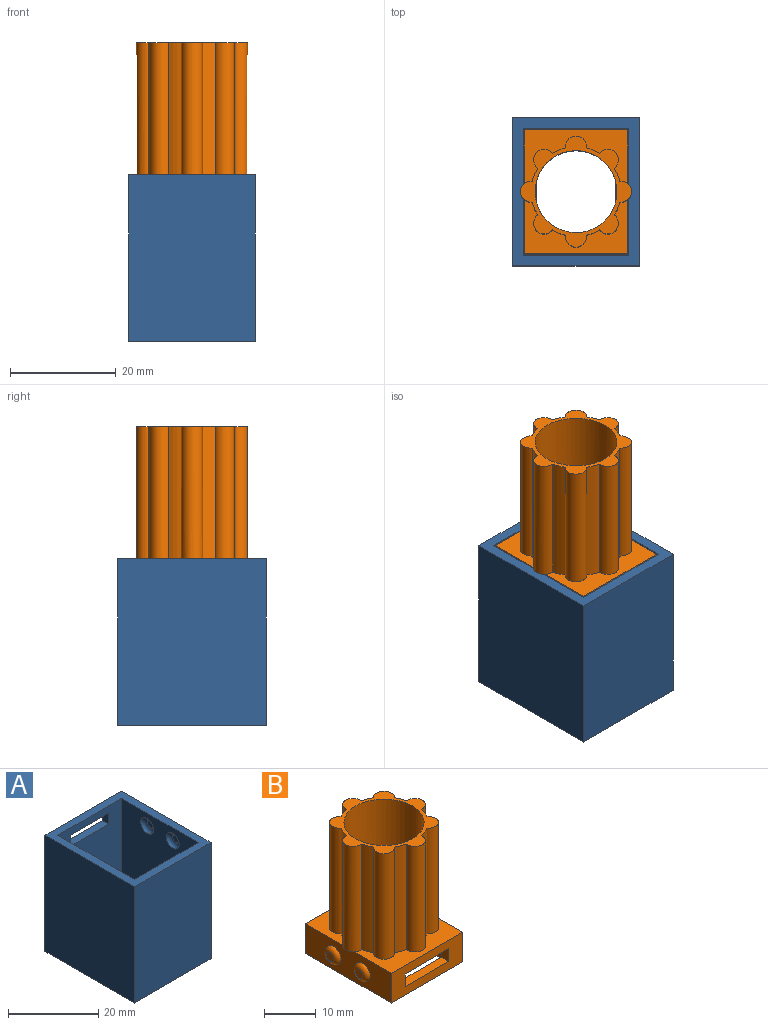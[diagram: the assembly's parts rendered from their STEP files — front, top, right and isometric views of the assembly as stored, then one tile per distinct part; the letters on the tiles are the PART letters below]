
ASSEMBLY  parts=2 mates=1
PART A: 27 faces, bbox 24x28x31.5 mm
  f0: plane 24x20mm, normal (0,0,1), area 180mm2, adj f4,f5,f6,f7,f10,f11,f12,f13
  f1: plane 31.5x24mm, normal (0,-1,0), area 756mm2, adj f2,f8,f9,f14
  f2: plane 31.5x28mm, normal (1,0,0), area 882mm2, adj f1,f3,f9,f14
  f3: plane 31.5x24mm, normal (0,1,0), area 720mm2, adj f2,f8,f9,f14,f23,f24,f25,f26
  f4: plane 20x1.5mm, normal (-1,0,0), area 30mm2, adj f0,f5,f7,f9
  f5: plane 15x1.5mm, normal (0,1,0), area 22.5mm2, adj f0,f4,f6,f9
  f6: plane 20x1.5mm, normal (1,0,0), area 30mm2, adj f0,f5,f7,f9
  f7: plane 15x1.5mm, normal (0,-1,0), area 22.5mm2, adj f0,f4,f6,f9
  f8: plane 31.5x28mm, normal (-1,0,0), area 882mm2, adj f1,f3,f9,f14
  f9: plane 28x24mm, normal (0,0,-1), area 372mm2, adj f1,f2,f3,f4,f5,f6,f7,f8
  f10: plane 30x20mm, normal (0,-1,0), area 564mm2, adj f0,f11,f13,f14,f23,f24,f25,f26
  f11: plane 30x24mm, normal (-1,0,0), area 694.9mm2, adj f0,f10,f12,f14,f19,f20
  f12: plane 30x20mm, normal (0,1,0), area 600mm2, adj f0,f11,f13,f14
  f13: plane 30x24mm, normal (1,0,0), area 694.9mm2, adj f0,f10,f12,f14,f21,f22
  f14: plane 28x24mm, normal (0,0,1), area 192mm2, adj f1,f2,f3,f8,f10,f11,f12,f13
  f15: plane 2x2mm, normal (1,0,0), area 3.1mm2, adj f21
  f16: plane 2x2mm, normal (1,0,0), area 3.1mm2, adj f22
  f17: plane 2x2mm, normal (-1,0,0), area 3.1mm2, adj f19
  f18: plane 2x2mm, normal (-1,0,0), area 3.1mm2, adj f20
  f19: torus R=1mm, axis (-1,0,0), area 16.2mm2, adj f11,f17
  f20: torus R=1mm, axis (-1,0,0), area 16.2mm2, adj f11,f18
  f21: torus R=1mm, axis (1,0,0), area 16.2mm2, adj f13,f15
  f22: torus R=1mm, axis (1,0,0), area 16.2mm2, adj f13,f16
  f23: plane 3x2mm, normal (-1,0,0), area 6mm2, adj f3,f10,f24,f26
  f24: plane 12x2mm, normal (0,0,1), area 24mm2, adj f3,f10,f23,f25
  f25: plane 3x2mm, normal (1,0,0), area 6mm2, adj f3,f10,f24,f26
  f26: plane 12x2mm, normal (0,0,-1), area 24mm2, adj f3,f10,f23,f25
PART B: 47 faces, bbox 21.5x23.5x32 mm
  f0: plane 4.59x3.04mm, normal (0,0,-1), area 5.6mm2, adj f4,f9,f45
  f1: plane 15.5x5mm, normal (0,1,0), area 41.5mm2, adj f2,f4,f5,f12,f42,f43,f44
  f2: plane 15.5x5.04mm, normal (0,0,-1), area 33.1mm2, adj f1,f4,f5,f6,f42,f43,f46
  f3: plane 19.5x10.19mm, normal (0,0,1), area 90.9mm2, adj f6,f7,f10,f30,f31,f32,f33,f34
  f4: plane 19.5x7.5mm, normal (-1,0,0), area 119.2mm2, adj f0,f1,f2,f9,f12,f45,f46
  f5: plane 19.5x7.5mm, normal (1,0,0), area 119.2mm2, adj f1,f2,f9,f12,f21,f45,f46
  f6: plane 19.5x7mm, normal (0,-1,0), area 100.5mm2, adj f2,f3,f7,f10,f12,f42,f43,f44
  f7: plane 23.5x7mm, normal (1,0,0), area 139.4mm2, adj f3,f6,f8,f11,f12,f15,f16,f22
  f8: plane 19.5x7mm, normal (0,1,0), area 136.5mm2, adj f7,f10,f11,f12
  f9: plane 15.5x5.51mm, normal (0,-1,0), area 79.6mm2, adj f0,f4,f5,f12,f21,f45
  f10: plane 23.5x7mm, normal (-1,0,0), area 139.4mm2, adj f3,f6,f8,f11,f12,f19,f20,f40
  f11: plane 19.5x10.19mm, normal (0,0,1), area 90.9mm2, adj f7,f8,f10,f23,f24,f25,f26,f27
  f12: plane 23.5x19.5mm, normal (0,0,-1), area 156mm2, adj f1,f4,f5,f6,f7,f8,f9,f10
  f13: plane 2x2mm, normal (1,0,0), area 3.1mm2, adj f15
  f14: plane 2x2mm, normal (1,0,0), area 3.1mm2, adj f16
  f15: torus R=1mm, axis (1,0,0), area 16.2mm2, adj f7,f13
  f16: torus R=1mm, axis (1,0,0), area 16.2mm2, adj f7,f14
  f17: plane 2x2mm, normal (-1,0,0), area 3.1mm2, adj f20
  f18: plane 2x2mm, normal (-1,0,0), area 3.1mm2, adj f19
  f19: torus R=1mm, axis (-1,0,0), area 16.2mm2, adj f10,f18
  f20: torus R=1mm, axis (-1,0,0), area 16.2mm2, adj f10,f17
  f21: plane 4.59x3.04mm, normal (0,0,-1), area 5.6mm2, adj f5,f9,f45
  f22: plane 3.12x0.75mm, normal (0,0,-1), area 1.6mm2, adj f7,f38
  f23: cylinder r=8.5mm len=25mm, axis (0,0,-1), area 66.7mm2, adj f11,f24,f38,f39
  f24: cylinder r=2mm len=25mm, axis (0,0,-1), area 168.9mm2, adj f11,f23,f25,f39
  f25: cylinder r=8.5mm len=25mm, axis (0,0,-1), area 66.7mm2, adj f11,f24,f26,f39
  f26: cylinder r=2mm len=25mm, axis (0,0,-1), area 168.9mm2, adj f11,f25,f27,f39
  f27: cylinder r=8.5mm len=25mm, axis (0,0,-1), area 66.7mm2, adj f11,f26,f28,f39
  f28: cylinder r=2mm len=25mm, axis (0,0,-1), area 168.9mm2, adj f11,f27,f29,f39
  f29: cylinder r=8.5mm len=25mm, axis (0,0,-1), area 66.7mm2, adj f11,f28,f30,f39
  f30: cylinder r=2mm len=25mm, axis (0,0,-1), area 168.9mm2, adj f3,f11,f29,f31,f39,f40
  f31: cylinder r=8.5mm len=25mm, axis (0,0,-1), area 66.7mm2, adj f3,f30,f32,f39
  f32: cylinder r=2mm len=25mm, axis (0,0,-1), area 168.9mm2, adj f3,f31,f33,f39
  f33: cylinder r=8.5mm len=25mm, axis (0,0,-1), area 66.7mm2, adj f3,f32,f34,f39
  f34: cylinder r=2mm len=25mm, axis (0,0,-1), area 168.9mm2, adj f3,f33,f35,f39
  f35: cylinder r=8.5mm len=25mm, axis (0,0,-1), area 66.7mm2, adj f3,f34,f36,f39
  f36: cylinder r=2mm len=25mm, axis (0,0,-1), area 168.9mm2, adj f3,f35,f37,f39
  f37: cylinder r=8.5mm len=25mm, axis (0,0,-1), area 66.7mm2, adj f3,f36,f38,f39
  f38: cylinder r=2mm len=25mm, axis (0,0,-1), area 168.9mm2, adj f3,f11,f22,f23,f37,f39
  f39: plane 21x21mm, normal (0,0,1), area 91.1mm2, adj f23,f24,f25,f26,f27,f28,f29,f30
  f40: plane 3.12x0.75mm, normal (0,0,-1), area 1.6mm2, adj f10,f30
  f41: cylinder r=7.75mm len=24.5mm, axis (0,0,-1), area 1193mm2, adj f39,f45,f46
  f42: plane 3x2mm, normal (-1,0,0), area 6mm2, adj f1,f2,f6,f44
  f43: plane 3x2mm, normal (1,0,0), area 6mm2, adj f1,f2,f6,f44
  f44: plane 12x2mm, normal (0,0,1), area 24mm2, adj f1,f6,f42,f43
  f45: cone r=7.75mm half-angle=45deg, axis (0,0,-1), area 64.5mm2, adj f0,f4,f5,f9,f21,f41
  f46: cone r=7.75mm half-angle=45deg, axis (0,0,-1), area 67.5mm2, adj f2,f4,f5,f41
PLACE A at identity
PLACE B rot(axis=(0,0,1),180deg) t=(0,0,24.5)mm
MATE fastened B.f23 <-> A.f14  axis (0,0,-1) through (0,0,31.5)mm
